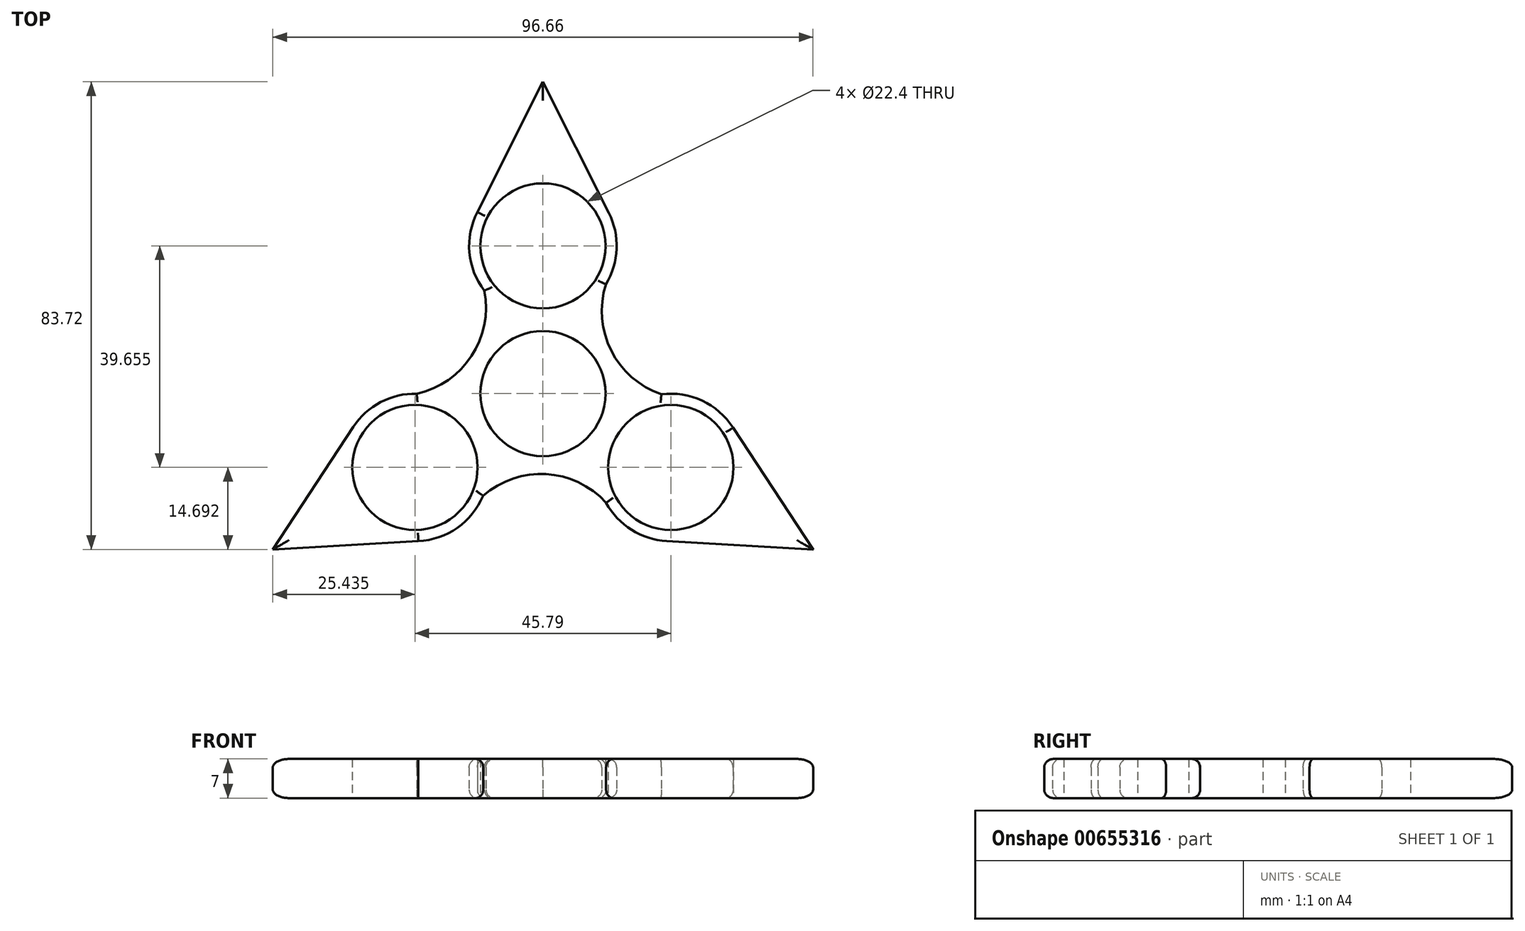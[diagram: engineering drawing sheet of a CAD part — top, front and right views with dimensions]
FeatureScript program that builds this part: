
annotation { "Feature Type Name" : "Feature", "Feature Type Description" : "" }
export const myFeature = defineFeature(function(context is Context, id is Id, definition is map)
    precondition{}
    {
        {
            var Q0;
            Q0=qCreatedBy(makeId("Top.planeOp"),FACE);
            var sketch = newSketch(context, id + "F0", { "sketchPlane" : qUnion([Q0])});
            skCircle(sketch, "E0", {"center": v(0, 0) * mm, "radius": 11.2 * mm});
            skCircle(sketch, "E1", {"center": v(0, 26.44) * mm, "radius": 11.2 * mm});
            skArc(sketch, "E2", {"start": v(11.27, 19.56) * mm, "mid": v(13.19, 25.9) * mm, "end": v(11.8, 32.37) * mm});
            skCircle(sketch, "E3.1.0", {"center": v(-22.9, -13.22) * mm, "radius": 11.2 * mm});
            skArc(sketch, "E3.1.1", {"start": v(-22.58, -0.02) * mm, "mid": v(-29.02, -1.53) * mm, "end": v(-33.93, -5.97) * mm});
            skCircle(sketch, "E3.2.0", {"center": v(22.9, -13.22) * mm, "radius": 11.2 * mm});
            skArc(sketch, "E3.2.1", {"start": v(11.3, -19.54) * mm, "mid": v(15.83, -24.37) * mm, "end": v(22.14, -26.4) * mm});
            skLineSegment(sketch, "E4", {"start": v(-11.72, 32.5) * mm, "end": v(0, 55.81) * mm});
            skLineSegment(sketch, "E5", {"start": v(0, 55.81) * mm, "end": v(11.8, 32.37) * mm});
            skLineSegment(sketch, "E6.1.0", {"start": v(-22.29, -26.4) * mm, "end": v(-48.33, -27.9) * mm});
            skLineSegment(sketch, "E6.1.1", {"start": v(-48.33, -27.9) * mm, "end": v(-33.93, -5.97) * mm});
            skLineSegment(sketch, "E6.2.0", {"start": v(34.01, -6.1) * mm, "end": v(48.33, -27.9) * mm});
            skLineSegment(sketch, "E6.2.1", {"start": v(48.33, -27.9) * mm, "end": v(22.14, -26.4) * mm});
            skArc(sketch, "E7", {"start": v(11.27, 19.56) * mm, "mid": v(12.21, 7.7) * mm, "end": v(21.2, -0.13) * mm});
            skArc(sketch, "E8.1.0", {"start": v(-22.58, -0.02) * mm, "mid": v(-12.77, 6.73) * mm, "end": v(-10.49, 18.42) * mm});
            skArc(sketch, "E8.2.0", {"start": v(11.3, -19.54) * mm, "mid": v(0.56, -14.42) * mm, "end": v(-10.7, -18.3) * mm});
            skArc(sketch, "E9.trimOffspring", {"start": v(-11.72, 32.5) * mm, "mid": v(-13.15, 25.28) * mm, "end": v(-10.49, 18.42) * mm});
            skArc(sketch, "E10.trimOffspring", {"start": v(-22.29, -26.4) * mm, "mid": v(-15.32, -24.03) * mm, "end": v(-10.7, -18.3) * mm});
            skArc(sketch, "E11.trimOffspring", {"start": v(34.01, -6.1) * mm, "mid": v(28.47, -1.25) * mm, "end": v(21.2, -0.13) * mm});
            skSolve(sketch);
        }
        {
            var Q0;
            Q0=makeQuery(id+"F0.imprint","IMPRINT",FACE,{"disambiguationData":[TD([[makeQuery(id+"F0.imprint","IMPRINT",EDGE,{"derivedFrom":sQuery(id+"F0.wireOp",EDGE,"E0")}),-1.0]])]});
            extrude(context, id + "F1", {"entities" : qUnion([Q0]), "depth" : 7 * mm, "offsetDistance" : 25 * mm});
        }
        {
            var Q0;
            Q0=makeQuery(id+"F1.opExtrude","CAP_EDGE",EDGE,{"disambiguationData":[OSD([sQuery(id+"F0.wireOp",EDGE,"E6.1.0")])],"isStart":false});
            var Q1;
            Q1=makeQuery(id+"F1.opExtrude","CAP_EDGE",EDGE,{"disambiguationData":[OSD([sQuery(id+"F0.wireOp",EDGE,"E10.trimOffspring")])],"isStart":false});
            var Q2;
            Q2=makeQuery(id+"F1.opExtrude","CAP_EDGE",EDGE,{"disambiguationData":[OSD([sQuery(id+"F0.wireOp",EDGE,"E6.1.1")])],"isStart":false});
            var Q3;
            Q3=makeQuery(id+"F1.opExtrude","CAP_EDGE",EDGE,{"disambiguationData":[OSD([sQuery(id+"F0.wireOp",EDGE,"E3.1.1")])],"isStart":false});
            var Q4;
            Q4=makeQuery(id+"F1.opExtrude","CAP_EDGE",EDGE,{"disambiguationData":[OSD([sQuery(id+"F0.wireOp",EDGE,"E8.1.0")])],"isStart":false});
            var Q5;
            Q5=makeQuery(id+"F1.opExtrude","CAP_EDGE",EDGE,{"disambiguationData":[OSD([sQuery(id+"F0.wireOp",EDGE,"E9.trimOffspring")])],"isStart":false});
            var Q6;
            Q6=makeQuery(id+"F1.opExtrude","CAP_EDGE",EDGE,{"disambiguationData":[OSD([sQuery(id+"F0.wireOp",EDGE,"E4")])],"isStart":false});
            var Q7;
            Q7=makeQuery(id+"F1.opExtrude","CAP_EDGE",EDGE,{"disambiguationData":[OSD([sQuery(id+"F0.wireOp",EDGE,"E5")])],"isStart":false});
            var Q8;
            Q8=makeQuery(id+"F1.opExtrude","CAP_EDGE",EDGE,{"disambiguationData":[OSD([sQuery(id+"F0.wireOp",EDGE,"E2")])],"isStart":false});
            var Q9;
            Q9=makeQuery(id+"F1.opExtrude","CAP_EDGE",EDGE,{"disambiguationData":[OSD([sQuery(id+"F0.wireOp",EDGE,"E7")])],"isStart":false});
            var Q10;
            Q10=makeQuery(id+"F1.opExtrude","CAP_EDGE",EDGE,{"disambiguationData":[OSD([sQuery(id+"F0.wireOp",EDGE,"E11.trimOffspring")])],"isStart":false});
            var Q11;
            Q11=makeQuery(id+"F1.opExtrude","CAP_EDGE",EDGE,{"disambiguationData":[OSD([sQuery(id+"F0.wireOp",EDGE,"E6.2.0")])],"isStart":false});
            var Q12;
            Q12=makeQuery(id+"F1.opExtrude","CAP_EDGE",EDGE,{"disambiguationData":[OSD([sQuery(id+"F0.wireOp",EDGE,"E8.2.0")])],"isStart":false});
            var Q13;
            Q13=makeQuery(id+"F1.opExtrude","CAP_EDGE",EDGE,{"disambiguationData":[OSD([sQuery(id+"F0.wireOp",EDGE,"E3.2.1")])],"isStart":false});
            var Q14;
            Q14=makeQuery(id+"F1.opExtrude","CAP_EDGE",EDGE,{"disambiguationData":[OSD([sQuery(id+"F0.wireOp",EDGE,"E6.2.1")])],"isStart":false});
            fillet(context, id + "F2", {"entities" : qUnion([Q0, Q1, Q2, Q3, Q4, Q5, Q6, Q7, Q8, Q9, Q10, Q11, Q12, Q13, Q14]), "radius" : 1.5 * mm, "tangentPropagation" : true, "allowEdgeOverflow" : false});
        }
        {
            var Q0;
            Q0=makeQuery(id+"F1.opExtrude","CAP_EDGE",EDGE,{"disambiguationData":[OSD([sQuery(id+"F0.wireOp",EDGE,"E6.1.1")])],"isStart":true});
            var Q1;
            Q1=makeQuery(id+"F1.opExtrude","CAP_EDGE",EDGE,{"disambiguationData":[OSD([sQuery(id+"F0.wireOp",EDGE,"E6.1.0")])],"isStart":true});
            var Q2;
            Q2=makeQuery(id+"F1.opExtrude","CAP_EDGE",EDGE,{"disambiguationData":[OSD([sQuery(id+"F0.wireOp",EDGE,"E3.1.1")])],"isStart":true});
            var Q3;
            Q3=makeQuery(id+"F1.opExtrude","CAP_EDGE",EDGE,{"disambiguationData":[OSD([sQuery(id+"F0.wireOp",EDGE,"E8.1.0")])],"isStart":true});
            var Q4;
            Q4=makeQuery(id+"F1.opExtrude","CAP_EDGE",EDGE,{"disambiguationData":[OSD([sQuery(id+"F0.wireOp",EDGE,"E10.trimOffspring")])],"isStart":true});
            var Q5;
            Q5=makeQuery(id+"F1.opExtrude","CAP_EDGE",EDGE,{"disambiguationData":[OSD([sQuery(id+"F0.wireOp",EDGE,"E8.2.0")])],"isStart":true});
            var Q6;
            Q6=makeQuery(id+"F1.opExtrude","CAP_EDGE",EDGE,{"disambiguationData":[OSD([sQuery(id+"F0.wireOp",EDGE,"E7")])],"isStart":true});
            var Q7;
            Q7=makeQuery(id+"F1.opExtrude","CAP_EDGE",EDGE,{"disambiguationData":[OSD([sQuery(id+"F0.wireOp",EDGE,"E9.trimOffspring")])],"isStart":true});
            var Q8;
            Q8=makeQuery(id+"F1.opExtrude","CAP_EDGE",EDGE,{"disambiguationData":[OSD([sQuery(id+"F0.wireOp",EDGE,"E4")])],"isStart":true});
            var Q9;
            Q9=makeQuery(id+"F1.opExtrude","CAP_EDGE",EDGE,{"disambiguationData":[OSD([sQuery(id+"F0.wireOp",EDGE,"E5")])],"isStart":true});
            var Q10;
            Q10=makeQuery(id+"F1.opExtrude","CAP_EDGE",EDGE,{"disambiguationData":[OSD([sQuery(id+"F0.wireOp",EDGE,"E2")])],"isStart":true});
            var Q11;
            Q11=makeQuery(id+"F1.opExtrude","CAP_EDGE",EDGE,{"disambiguationData":[OSD([sQuery(id+"F0.wireOp",EDGE,"E11.trimOffspring")])],"isStart":true});
            var Q12;
            Q12=makeQuery(id+"F1.opExtrude","CAP_EDGE",EDGE,{"disambiguationData":[OSD([sQuery(id+"F0.wireOp",EDGE,"E3.2.1")])],"isStart":true});
            var Q13;
            Q13=makeQuery(id+"F1.opExtrude","CAP_EDGE",EDGE,{"disambiguationData":[OSD([sQuery(id+"F0.wireOp",EDGE,"E6.2.1")])],"isStart":true});
            fillet(context, id + "F3", {"entities" : qUnion([Q0, Q1, Q2, Q3, Q4, Q5, Q6, Q7, Q8, Q9, Q10, Q11, Q12, Q13]), "radius" : 1.5 * mm, "tangentPropagation" : true, "allowEdgeOverflow" : false});
        }
    });
